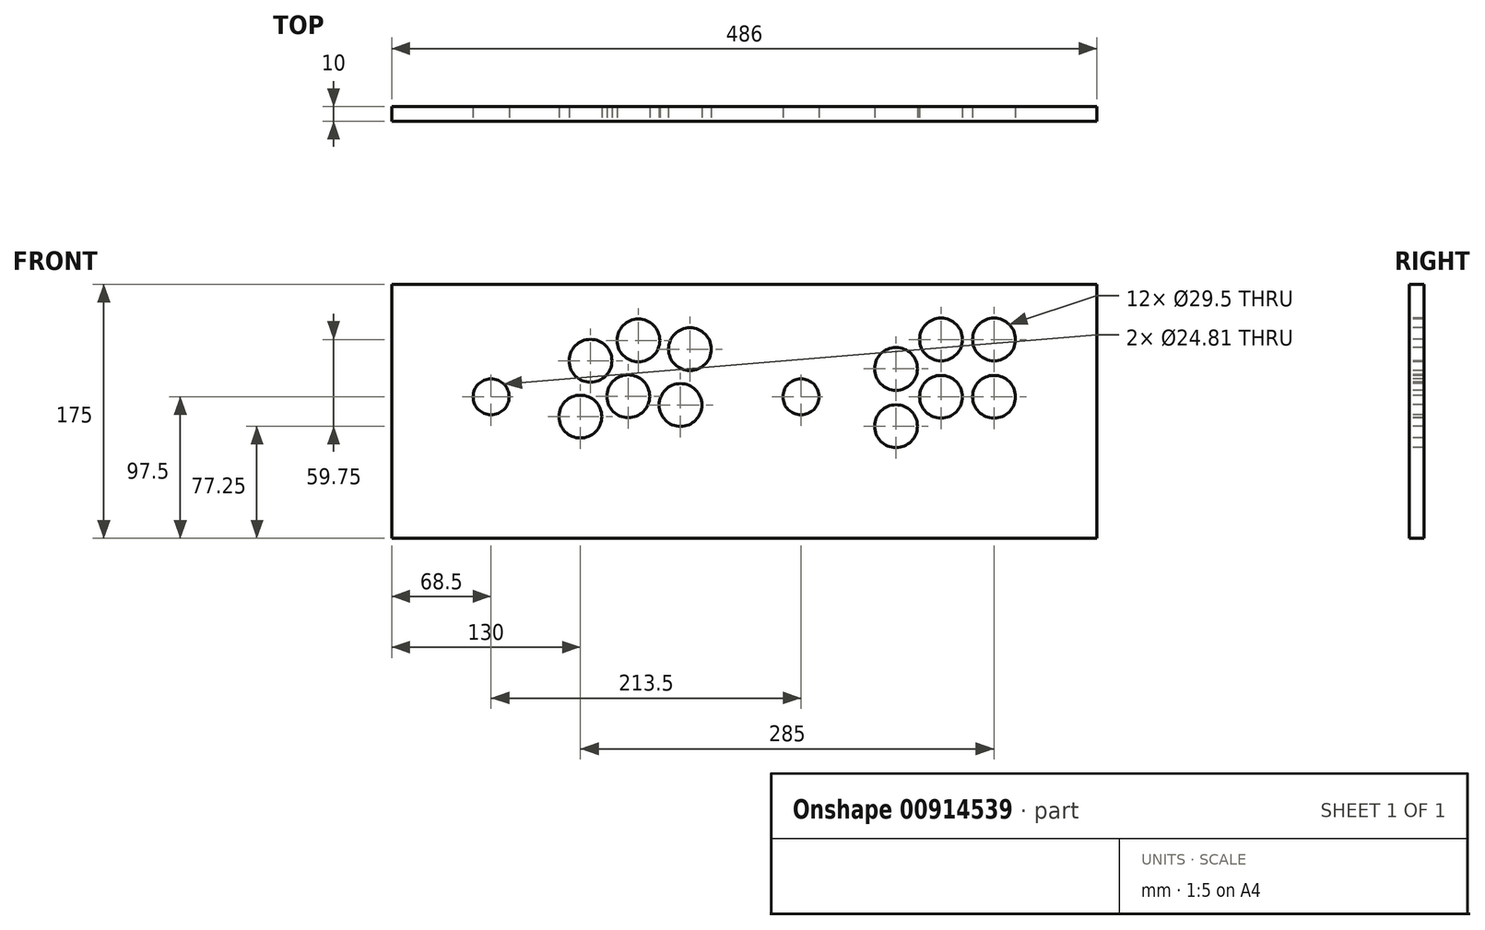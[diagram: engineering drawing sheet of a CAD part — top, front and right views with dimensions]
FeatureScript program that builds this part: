
annotation { "Feature Type Name" : "Feature", "Feature Type Description" : "" }
export const myFeature = defineFeature(function(context is Context, id is Id, definition is map)
    precondition{}
    {
        {
            var Q0;
            Q0=qCreatedBy(makeId("Front.planeOp"),FACE);
            var sketch = newSketch(context, id + "F0", { "sketchPlane" : qUnion([Q0])});
            skLineSegment(sketch, "E0.bottom", {"start": v(0, 0) * mm, "end": v(486, 0) * mm});
            skLineSegment(sketch, "E0.top", {"start": v(0, 175) * mm, "end": v(486, 175) * mm});
            skLineSegment(sketch, "E0.left", {"start": v(0, 0) * mm, "end": v(0, 175) * mm});
            skLineSegment(sketch, "E0.right", {"start": v(486, 0) * mm, "end": v(486, 175) * mm});
            skSolve(sketch);
        }
        {
            var Q0;
            Q0=qSketchRegion(id+"F0",true);
            var Q1;
            Q1=qSketchRegion(id+"F4",true);
            extrude(context, id + "F1", {"entities" : qUnion([Q0, Q1]), "depth" : 10 * mm, "offsetDistance" : 25 * mm});
        }
        {
            var Q0;
            Q0=makeQuery(id+"F1.opExtrude","CAP_FACE",FACE,{"disambiguationData":[OSD([sQuery(id+"F0.wireOp",EDGE,"E0.bottom"),sQuery(id+"F0.wireOp",EDGE,"E0.top"),sQuery(id+"F0.wireOp",EDGE,"E0.left"),sQuery(id+"F0.wireOp",EDGE,"E0.right")])],"isStart":false});
            var sketch = newSketch(context, id + "F2", { "sketchPlane" : qUnion([Q0])});
            skLineSegment(sketch, "E1", {"start": v(19.6, 30.97) * mm, "end": v(224.1, 30.97) * mm});
            skSolve(sketch);
        }
        {
            var Q0;
            Q0=makeQuery(id+"F2.imprint","IMPRINT",FACE,{"disambiguationData":[TD([[makeQuery(id+"F2.imprint","IMPRINT",EDGE,{"derivedFrom":makeQuery(id+"F1.opExtrude","CAP_EDGE",EDGE,{"disambiguationData":[OSD([sQuery(id+"F0.wireOp",EDGE,"E0.bottom")])],"isStart":false})}),1.0]])]});
            var sketch = newSketch(context, id + "F3", { "sketchPlane" : qUnion([Q0])});
            skCircle(sketch, "E2", {"center": v(170, 136.34) * mm, "radius": 14.75 * mm});
            skCircle(sketch, "E3", {"center": v(205.5, 130.34) * mm, "radius": 14.75 * mm});
            skCircle(sketch, "E4", {"center": v(199, 91.84) * mm, "radius": 14.75 * mm});
            skCircle(sketch, "E5", {"center": v(163, 97.84) * mm, "radius": 14.75 * mm});
            skCircle(sketch, "E6", {"center": v(130, 83.84) * mm, "radius": 14.75 * mm});
            skCircle(sketch, "E7", {"center": v(137, 122.34) * mm, "radius": 14.75 * mm});
            skCircle(sketch, "E8", {"center": v(68.5, 97.5) * mm, "radius": 12.4 * mm});
            skSolve(sketch);
        }
        {
            var Q0;
            Q0=makeQuery(id+"F1.opExtrude","CAP_FACE",FACE,{"disambiguationData":[OSD([sQuery(id+"F0.wireOp",EDGE,"E0.bottom"),sQuery(id+"F0.wireOp",EDGE,"E0.top"),sQuery(id+"F0.wireOp",EDGE,"E0.left"),sQuery(id+"F0.wireOp",EDGE,"E0.right")])],"isStart":false});
            var sketch = newSketch(context, id + "F4", { "sketchPlane" : qUnion([Q0])});
            skLineSegment(sketch, "E9", {"start": v(258.96, 30.87) * mm, "end": v(457.96, 30.87) * mm});
            skSolve(sketch);
        }
        {
            var Q0;
            Q0=makeQuery(id+"F1.opExtrude","CAP_FACE",FACE,{"disambiguationData":[OSD([sQuery(id+"F0.wireOp",EDGE,"E0.bottom"),sQuery(id+"F0.wireOp",EDGE,"E0.top"),sQuery(id+"F0.wireOp",EDGE,"E0.left"),sQuery(id+"F0.wireOp",EDGE,"E0.right")])],"isStart":false});
            var sketch = newSketch(context, id + "F5", { "sketchPlane" : qUnion([Q0])});
            skCircle(sketch, "E10", {"center": v(347.5, 116.75) * mm, "radius": 14.75 * mm});
            skCircle(sketch, "E11", {"center": v(378.5, 137) * mm, "radius": 14.75 * mm});
            skCircle(sketch, "E12", {"center": v(415, 137) * mm, "radius": 14.75 * mm});
            skCircle(sketch, "E13", {"center": v(415, 97.5) * mm, "radius": 14.75 * mm});
            skCircle(sketch, "E14", {"center": v(378.5, 97.5) * mm, "radius": 14.75 * mm});
            skCircle(sketch, "E15", {"center": v(347.5, 77.25) * mm, "radius": 14.75 * mm});
            skCircle(sketch, "E16", {"center": v(282, 97.5) * mm, "radius": 12.4 * mm});
            skSolve(sketch);
        }
        {
            var Q0;
            Q0=makeQuery(id+"F3.imprint","IMPRINT",FACE,{"disambiguationData":[TD([[makeQuery(id+"F3.imprint","IMPRINT",EDGE,{"derivedFrom":sQuery(id+"F3.wireOp",EDGE,"E2")}),-1.0]])]});
            var sketch = newSketch(context, id + "F6", { "sketchPlane" : qUnion([Q0])});
            skCircle(sketch, "E17", {"center": v(254, 145) * mm, "radius": 14 * mm});
            skCircle(sketch, "E18", {"center": v(50, 145) * mm, "radius": 14 * mm});
            skCircle(sketch, "E19", {"center": v(90, 145) * mm, "radius": 14 * mm});
            skCircle(sketch, "E20", {"center": v(294, 145) * mm, "radius": 14 * mm});
            skCircle(sketch, "E21", {"center": v(446, 145) * mm, "radius": 14 * mm});
            skSolve(sketch);
        }
        {
            var Q0;
            Q0=makeQuery(id+"F5.imprint","IMPRINT",FACE,{"disambiguationData":[TD([[makeQuery(id+"F5.imprint","IMPRINT",EDGE,{"derivedFrom":sQuery(id+"F5.wireOp",EDGE,"E10")}),1.0]])]});
            var Q1;
            Q1=makeQuery(id+"F5.imprint","IMPRINT",FACE,{"disambiguationData":[TD([[makeQuery(id+"F5.imprint","IMPRINT",EDGE,{"derivedFrom":sQuery(id+"F5.wireOp",EDGE,"E11")}),1.0]])]});
            var Q2;
            Q2=makeQuery(id+"F5.imprint","IMPRINT",FACE,{"disambiguationData":[TD([[makeQuery(id+"F5.imprint","IMPRINT",EDGE,{"derivedFrom":sQuery(id+"F5.wireOp",EDGE,"E12")}),1.0]])]});
            var Q3;
            Q3=makeQuery(id+"F5.imprint","IMPRINT",FACE,{"disambiguationData":[TD([[makeQuery(id+"F5.imprint","IMPRINT",EDGE,{"derivedFrom":sQuery(id+"F5.wireOp",EDGE,"E13")}),1.0]])]});
            var Q4;
            Q4=makeQuery(id+"F5.imprint","IMPRINT",FACE,{"disambiguationData":[TD([[makeQuery(id+"F5.imprint","IMPRINT",EDGE,{"derivedFrom":sQuery(id+"F5.wireOp",EDGE,"E14")}),1.0]])]});
            var Q5;
            Q5=makeQuery(id+"F5.imprint","IMPRINT",FACE,{"disambiguationData":[TD([[makeQuery(id+"F5.imprint","IMPRINT",EDGE,{"derivedFrom":sQuery(id+"F5.wireOp",EDGE,"E15")}),1.0]])]});
            var Q6;
            Q6=makeQuery(id+"F5.imprint","IMPRINT",FACE,{"disambiguationData":[TD([[makeQuery(id+"F5.imprint","IMPRINT",EDGE,{"derivedFrom":sQuery(id+"F5.wireOp",EDGE,"E16")}),1.0]])]});
            extrude(context, id + "F7", {"entities" : qUnion([Q0, Q1, Q2, Q3, Q4, Q5, Q6]), "operationType" : NewBodyOperationType.REMOVE, "oppositeDirection" : true, "depth" : 25 * mm, "offsetDistance" : 25 * mm});
        }
        {
            var Q0;
            Q0=qSketchRegion(id+"F3",true);
            extrude(context, id + "F8", {"entities" : qUnion([Q0]), "operationType" : NewBodyOperationType.REMOVE, "oppositeDirection" : true, "depth" : 25 * mm, "offsetDistance" : 25 * mm});
        }
    });
